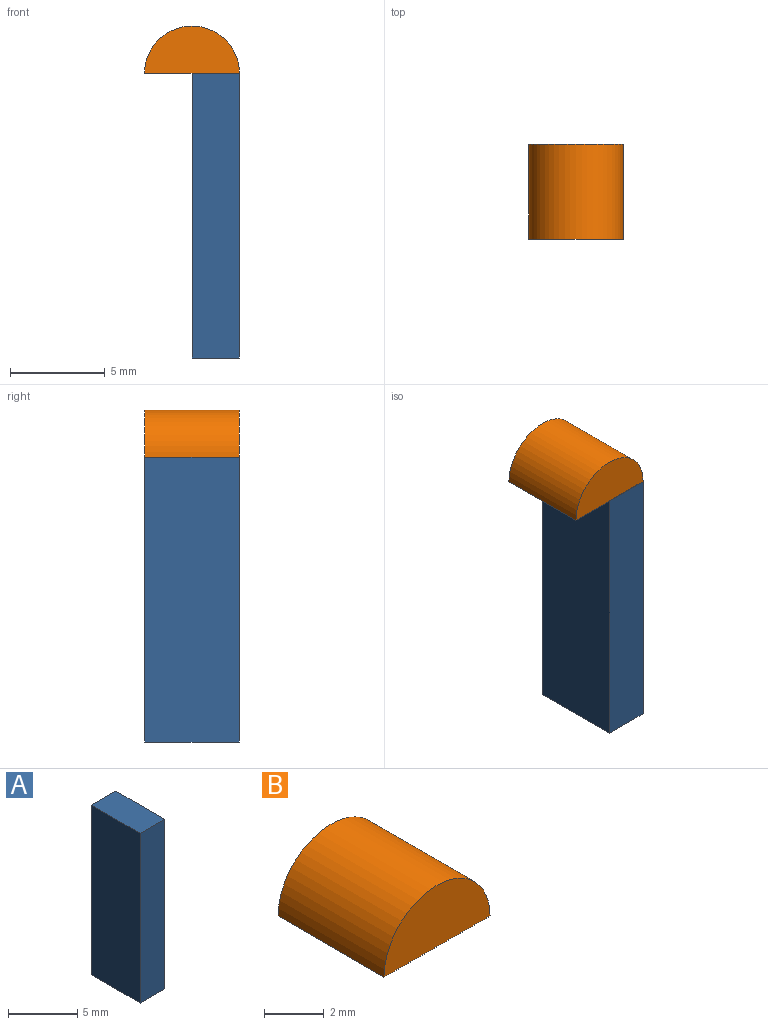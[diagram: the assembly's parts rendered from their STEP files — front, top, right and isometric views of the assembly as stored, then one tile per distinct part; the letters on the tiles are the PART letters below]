
ASSEMBLY  parts=2 mates=1
PART A: 6 faces, bbox 2.5x5x15 mm
  f0: plane 15x5mm, normal (-1,0,0), area 75mm2, adj f1,f3,f4,f5
  f1: plane 5x2.5mm, normal (0,0,-1), area 12.5mm2, adj f0,f2,f4,f5
  f2: plane 15x5mm, normal (1,0,0), area 75mm2, adj f1,f3,f4,f5
  f3: plane 5x2.5mm, normal (0,0,1), area 12.5mm2, adj f0,f2,f4,f5
  f4: plane 15x2.5mm, normal (0,-1,0), area 37.5mm2, adj f0,f1,f2,f3
  f5: plane 15x2.5mm, normal (0,1,0), area 37.5mm2, adj f0,f1,f2,f3
PART B: 4 faces, bbox 5x5x2.5 mm
  f0: cylinder r=2.5mm len=5mm, axis (0,1,0), area 39.3mm2, adj f1,f2,f3
  f1: plane 5x2.5mm, normal (0,-1,0), area 9.8mm2, adj f0,f3
  f2: plane 5x2.5mm, normal (0,1,0), area 9.8mm2, adj f0,f3
  f3: plane 5x5mm, normal (0,0,-1), area 25mm2, adj f0,f1,f2
PLACE A t=(0,-5.88,-10.49)mm
PLACE B t=(0,-5.88,4.51)mm
MATE fastened A.f3 <-> B.f3  axis (0,0,1) through (2.5,-5.88,4.51)mm
